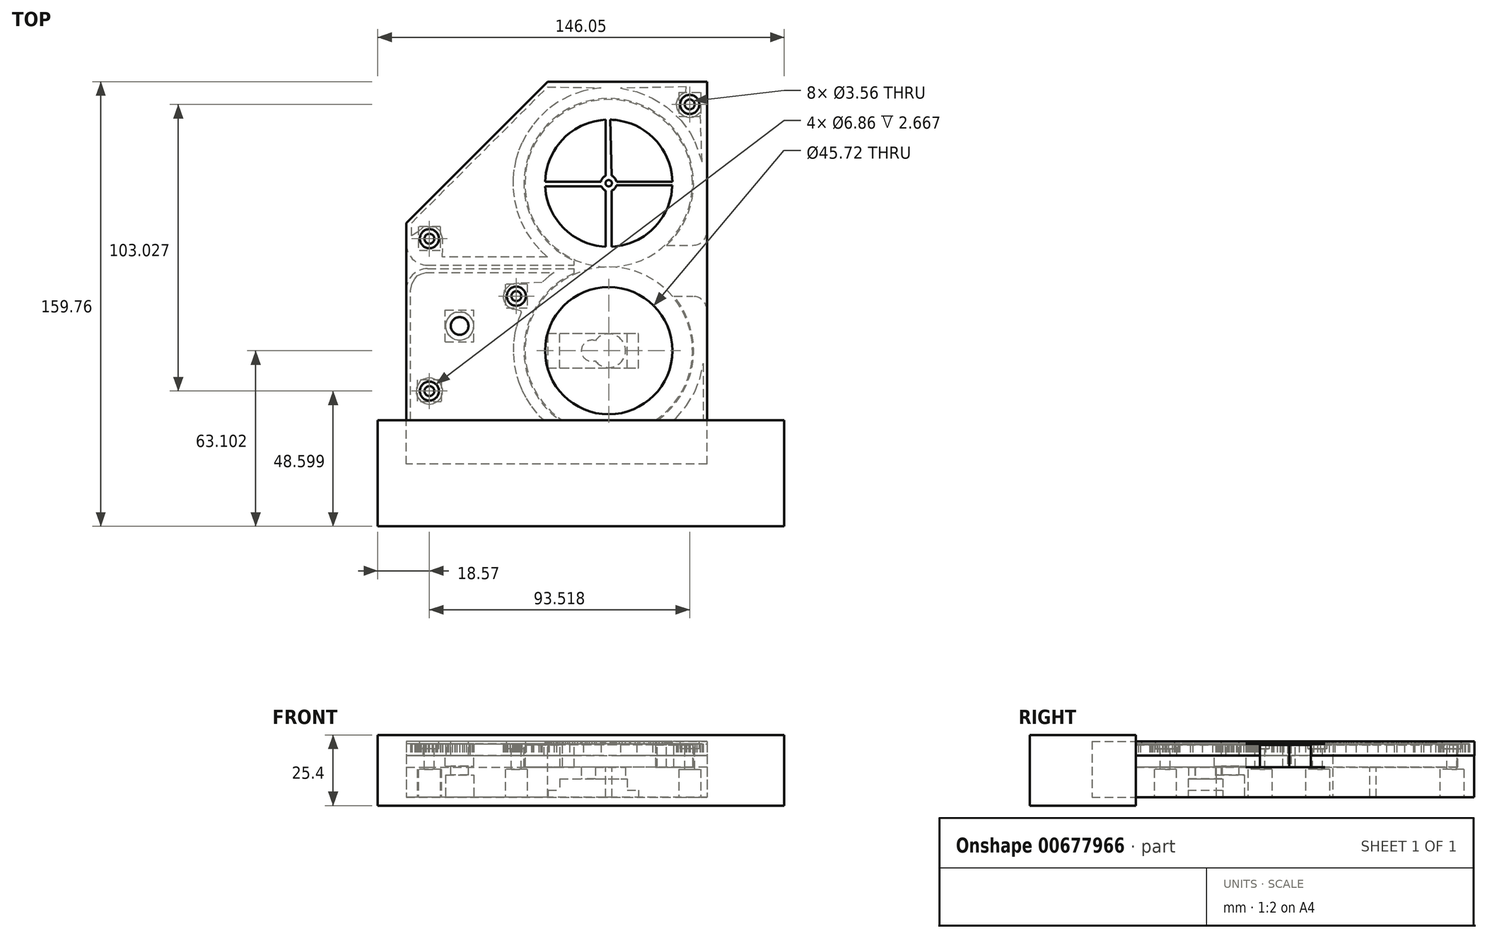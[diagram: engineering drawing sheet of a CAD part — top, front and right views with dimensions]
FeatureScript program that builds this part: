
annotation { "Feature Type Name" : "Feature", "Feature Type Description" : "" }
export const myFeature = defineFeature(function(context is Context, id is Id, definition is map)
    precondition{}
    {
        {
            var Q0;
            Q0=qCreatedBy(makeId("Top.planeOp"),FACE);
            var sketch = newSketch(context, id + "F0", { "sketchPlane" : qUnion([Q0])});
            skLineSegment(sketch, "E0.bottom", {"start": v(35.3, 36.28) * mm, "end": v(-72.74, 36.28) * mm});
            skLineSegment(sketch, "E0.top", {"start": v(35.3, -100.69) * mm, "end": v(-72.74, -100.69) * mm});
            skLineSegment(sketch, "E0.left", {"start": v(35.3, 36.28) * mm, "end": v(35.3, -100.69) * mm});
            skLineSegment(sketch, "E0.right", {"start": v(-72.74, 36.28) * mm, "end": v(-72.74, -100.69) * mm});
            skSolve(sketch);
        }
        {
            var Q0;
            Q0 = qSketchRegion(id + "F0", true);
            extrude(context, id + "F1", {"entities" : qUnion([Q0]), "depth" : 5.08 * mm, "offsetDistance" : 25.4 * mm});
        }
        {
            var Q0;
            {var subQ0=sQuery(id+"F0.wireOp",EDGE,"E0.right");var subQ1=sQuery(id+"F0.wireOp",EDGE,"E0.left");var subQ2=sQuery(id+"F0.wireOp",EDGE,"E0.top");Q0=makeQuery(id+"Ft3egFjg6mGKuU7_1.boolean.opBoolean","SPLIT",FACE,{"disambiguationData":[TD([makeQuery(id+"F1.opExtrude","SWEPT_FACE",FACE,{"disambiguationData":[OSD([subQ2])]})])],"derivedFrom":makeQuery(id+"F1.opExtrude","CAP_FACE",FACE,{"disambiguationData":[OSD([sQuery(id+"F0.wireOp",EDGE,"E0.bottom"),subQ2,subQ1,subQ0])],"isStart":false})});}
            var sketch = newSketch(context, id + "F2", { "sketchPlane" : qUnion([Q0])});
            skLineSegment(sketch, "E1.bottom", {"start": v(-72.74, -100.69) * mm, "end": v(35.3, -100.69) * mm});
            skLineSegment(sketch, "E1.top", {"start": v(-72.74, 36.46) * mm, "end": v(35.3, 36.46) * mm});
            skLineSegment(sketch, "E1.left", {"start": v(-72.74, -100.69) * mm, "end": v(-72.74, 36.46) * mm});
            skLineSegment(sketch, "E1.right", {"start": v(35.3, -100.69) * mm, "end": v(35.3, 36.46) * mm});
            skSolve(sketch);
        }
        {
            var Q0;
            Q0 = qSketchRegion(id + "F2", true);
            extrude(context, id + "F3", {"entities" : qUnion([Q0]), "depth" : 5.08 * mm, "offsetDistance" : 25.4 * mm});
        }
        {
            var Q0;
            Q0=makeQuery(id+"F1.opExtrude","CAP_FACE",FACE,{"disambiguationData":[OSD([sQuery(id+"F0.wireOp",EDGE,"E0.bottom"),sQuery(id+"F0.wireOp",EDGE,"E0.top"),sQuery(id+"F0.wireOp",EDGE,"E0.left"),sQuery(id+"F0.wireOp",EDGE,"E0.right")])],"isStart":false});
            var sketch = newSketch(context, id + "F4", { "sketchPlane" : qUnion([Q0])});
            skCircle(sketch, "E2", {"center": v(0, 0) * mm, "radius": 30.48 * mm});
            skCircle(sketch, "E3", {"center": v(0, -60.2) * mm, "radius": 30.48 * mm});
            skLineSegment(sketch, "E4", {"start": v(0, 0) * mm, "end": v(0, -60.2) * mm});
            skSolve(sketch);
        }
        {
            var Q0;
            Q0 = qSketchRegion(id + "F4", true);
            extrude(context, id + "F5", {"entities" : qUnion([Q0]), "operationType" : NewBodyOperationType.REMOVE, "endBound" : BoundingType.SYMMETRIC, "oppositeDirection" : true, "depth" : 8.38 * mm, "offsetDistance" : 25.4 * mm});
        }
        {
            var Q0;
            Q0=makeQuery(id+"F1.opExtrude","SWEPT_EDGE",EDGE,{"disambiguationData":[OSD([sQuery(id+"F0.wireOp",EDGE,"E0.bottom"),sQuery(id+"F0.wireOp",EDGE,"E0.right")])]});
            chamfer(context, id + "F6", {"entities" : qUnion([Q0]), "width" : 50.8 * mm, "tangentPropagation" : true});
        }
        {
            var Q0;
            Q0=makeQuery(id+"F5.boolean.opBoolean","COPY",FACE,{"derivedFrom":makeQuery(id+"F5.opExtrude","CAP_FACE",FACE,{"disambiguationData":[OSD([sQuery(id+"F4.wireOp",EDGE,"E2")])],"isStart":false})});
            var sketch = newSketch(context, id + "F7", { "sketchPlane" : qUnion([Q0])});
            skCircle(sketch, "E5", {"center": v(0, 0) * mm, "radius": 1.14 * mm});
            skCircle(sketch, "E6", {"center": v(0, -60.2) * mm, "radius": 5.08 * mm});
            skLineSegment(sketch, "E7", {"start": v(0, 0) * mm, "end": v(0, -60.2) * mm});
            skSolve(sketch);
        }
        {
            var Q0;
            Q0 = qSketchRegion(id + "F7", true);
            extrude(context, id + "F8", {"entities" : qUnion([Q0]), "operationType" : NewBodyOperationType.REMOVE, "endBound" : BoundingType.SYMMETRIC, "oppositeDirection" : true, "depth" : 25.4 * mm, "offsetDistance" : 25.4 * mm});
        }
        {
            var Q0;
            Q0=makeQuery(id+"F3.opExtrude","SWEPT_EDGE",EDGE,{"disambiguationData":[OSD([sQuery(id+"F2.wireOp",EDGE,"E1.top"),sQuery(id+"F2.wireOp",EDGE,"E1.left")])]});
            chamfer(context, id + "F9", {"entities" : qUnion([Q0]), "width" : 50.8 * mm, "tangentPropagation" : true});
        }
        {
            var Q0;
            {var subQ0=sQuery(id+"F0.wireOp",EDGE,"E0.right");var subQ1=sQuery(id+"F0.wireOp",EDGE,"E0.left");var subQ2=sQuery(id+"F0.wireOp",EDGE,"E0.bottom");var subQ3=makeQuery(id+"F1.opExtrude","CAP_FACE",FACE,{"disambiguationData":[OSD([subQ2,sQuery(id+"F0.wireOp",EDGE,"E0.top"),subQ1,subQ0])],"isStart":false});Q0=makeQuery(id+"FFet9ike0QdHDJR_2.boolean.opBoolean","SPLIT",FACE,{"disambiguationData":[TD([makeQuery(id+"F1.opExtrude","SWEPT_FACE",FACE,{"disambiguationData":[OSD([subQ2])]})])],"derivedFrom":subQ3});}
            var sketch = newSketch(context, id + "F10", { "sketchPlane" : qUnion([Q0])});
            skLineSegment(sketch, "E8.bottom", {"start": v(0, -22.29) * mm, "end": v(46.56, -22.29) * mm});
            skLineSegment(sketch, "E8.top", {"start": v(0, -40.66) * mm, "end": v(46.56, -40.66) * mm});
            skLineSegment(sketch, "E8.left", {"start": v(0, -22.29) * mm, "end": v(0, -40.66) * mm});
            skLineSegment(sketch, "E8.right", {"start": v(46.56, -22.29) * mm, "end": v(46.56, -40.66) * mm});
            skLineSegment(sketch, "E9.bottom", {"start": v(2.73, -33.02) * mm, "end": v(-12.34, -33.02) * mm});
            skLineSegment(sketch, "E9.top", {"start": v(2.73, -27.18) * mm, "end": v(-12.34, -27.18) * mm});
            skLineSegment(sketch, "E9.left", {"start": v(2.73, -33.02) * mm, "end": v(2.73, -27.18) * mm});
            skLineSegment(sketch, "E9.right", {"start": v(-12.34, -33.02) * mm, "end": v(-12.34, -27.18) * mm});
            skPoint(sketch, "E9.middle", {"position": v(-4.8, -30.1) * mm});
            skSolve(sketch);
        }
        {
            var Q0;
            Q0 = qSketchRegion(id + "F10", true);
            extrude(context, id + "F11", {"entities" : qUnion([Q0]), "operationType" : NewBodyOperationType.REMOVE, "endBound" : BoundingType.SYMMETRIC, "oppositeDirection" : true, "depth" : 8.38 * mm, "offsetDistance" : 25.4 * mm});
        }
        {
            var Q0;
            Q0=makeQuery(id+"F1.opExtrude","CAP_FACE",FACE,{"disambiguationData":[OSD([sQuery(id+"F0.wireOp",EDGE,"E0.bottom"),sQuery(id+"F0.wireOp",EDGE,"E0.top"),sQuery(id+"F0.wireOp",EDGE,"E0.left"),sQuery(id+"F0.wireOp",EDGE,"E0.right")])],"isStart":true});
            extrude(context, id + "F12", {"entities" : qUnion([Q0]), "operationType" : NewBodyOperationType.ADD, "depth" : 9.9 * mm, "offsetDistance" : 25.4 * mm});
        }
        {
            var Q0;
            Q0=makeQuery(id+"F12.opExtrude","CAP_FACE",FACE,{"disambiguationData":[OSD([sQuery(id+"F0.wireOp",EDGE,"E0.bottom"),sQuery(id+"F0.wireOp",EDGE,"E0.top"),sQuery(id+"F0.wireOp",EDGE,"E0.left"),sQuery(id+"F0.wireOp",EDGE,"E0.right")])],"isStart":false});
            var sketch = newSketch(context, id + "F13", { "sketchPlane" : qUnion([Q0])});
            skPoint(sketch, "E10.middle", {"position": v(0, 60.2) * mm});
            skLineSegment(sketch, "E11", {"start": v(0, 60.2) * mm, "end": v(-5.49, 60.2) * mm});
            skLineSegment(sketch, "E12.bottom", {"start": v(-21.74, 66.42) * mm, "end": v(10.77, 66.42) * mm});
            skLineSegment(sketch, "E12.top", {"start": v(-21.74, 53.98) * mm, "end": v(10.77, 53.98) * mm});
            skLineSegment(sketch, "E12.left", {"start": v(-21.74, 66.42) * mm, "end": v(-21.74, 53.98) * mm});
            skLineSegment(sketch, "E12.right", {"start": v(10.77, 66.42) * mm, "end": v(10.77, 53.98) * mm});
            skPoint(sketch, "E12.middle", {"position": v(-5.49, 60.2) * mm});
            skSolve(sketch);
        }
        {
            var Q0;
            Q0 = qSketchRegion(id + "F13", true);
            extrude(context, id + "F14", {"entities" : qUnion([Q0]), "operationType" : NewBodyOperationType.REMOVE, "oppositeDirection" : true, "depth" : 2.54 * mm, "offsetDistance" : 25.4 * mm});
        }
        {
            var Q0;
            Q0=makeQuery(id+"F14.boolean.opBoolean","COPY",FACE,{"derivedFrom":makeQuery(id+"F14.opExtrude","CAP_FACE",FACE,{"disambiguationData":[OSD([sQuery(id+"F13.wireOp",EDGE,"E12.bottom"),sQuery(id+"F13.wireOp",EDGE,"E12.top"),sQuery(id+"F13.wireOp",EDGE,"E12.left"),sQuery(id+"F13.wireOp",EDGE,"E12.right")])],"isStart":false})});
            var sketch = newSketch(context, id + "F15", { "sketchPlane" : qUnion([Q0])});
            skCircle(sketch, "E13", {"center": v(0, 60.2) * mm, "radius": 6.03 * mm});
            skCircle(sketch, "E14", {"center": v(-6.03, 60.2) * mm, "radius": 3.81 * mm});
            skSolve(sketch);
        }
        {
            var Q0;
            Q0 = qSketchRegion(id + "F15", true);
            extrude(context, id + "F16", {"entities" : qUnion([Q0]), "operationType" : NewBodyOperationType.REMOVE, "oppositeDirection" : true, "depth" : 25.4 * mm, "offsetDistance" : 25.4 * mm});
        }
        {
            var Q0;
            {var subQ0=sQuery(id+"F0.wireOp",EDGE,"E0.right");var subQ1=sQuery(id+"F0.wireOp",EDGE,"E0.left");var subQ2=sQuery(id+"F0.wireOp",EDGE,"E0.top");var subQ3=makeQuery(id+"F1.opExtrude","CAP_FACE",FACE,{"disambiguationData":[OSD([sQuery(id+"F0.wireOp",EDGE,"E0.bottom"),subQ2,subQ1,subQ0])],"isStart":false});Q0=makeQuery(id+"FFet9ike0QdHDJR_2.boolean.opBoolean","SPLIT",FACE,{"disambiguationData":[TD([makeQuery(id+"F1.opExtrude","SWEPT_FACE",FACE,{"disambiguationData":[OSD([subQ2])]})])],"derivedFrom":subQ3});}
            var sketch = newSketch(context, id + "F17", { "sketchPlane" : qUnion([Q0])});
            skCircle(sketch, "E15", {"center": v(-33.19, -40.6) * mm, "radius": 1.78 * mm});
            skCircle(sketch, "E16", {"center": v(29.09, 28.33) * mm, "radius": 1.78 * mm});
            skCircle(sketch, "E17", {"center": v(-53.56, -51.3) * mm, "radius": 3.18 * mm});
            skCircle(sketch, "E18", {"center": v(-64.43, -19.95) * mm, "radius": 1.78 * mm});
            skCircle(sketch, "E19", {"center": v(-64.43, -74.7) * mm, "radius": 1.78 * mm});
            skSolve(sketch);
        }
        {
            var Q0;
            Q0 = qSketchRegion(id + "F17", true);
            extrude(context, id + "F18", {"entities" : qUnion([Q0]), "operationType" : NewBodyOperationType.REMOVE, "endBound" : BoundingType.SYMMETRIC, "oppositeDirection" : true, "depth" : 50.8 * mm, "offsetDistance" : 25.4 * mm});
        }
        {
            var Q0;
            Q0=makeQuery(id+"F3.opExtrude","CAP_FACE",FACE,{"disambiguationData":[OSD([sQuery(id+"F2.wireOp",EDGE,"E1.bottom"),sQuery(id+"F2.wireOp",EDGE,"E1.top"),sQuery(id+"F2.wireOp",EDGE,"E1.left"),sQuery(id+"F2.wireOp",EDGE,"E1.right")])],"isStart":false});
            var sketch = newSketch(context, id + "F19", { "sketchPlane" : qUnion([Q0])});
            skCircle(sketch, "E20", {"center": v(-33.19, -40.6) * mm, "radius": 3.43 * mm});
            skCircle(sketch, "E21", {"center": v(29.09, 28.33) * mm, "radius": 3.43 * mm});
            skCircle(sketch, "E22", {"center": v(-64.43, -19.95) * mm, "radius": 3.43 * mm});
            skCircle(sketch, "E23", {"center": v(-64.43, -74.7) * mm, "radius": 3.43 * mm});
            skSolve(sketch);
        }
        {
            var Q0;
            Q0 = qSketchRegion(id + "F19", true);
            extrude(context, id + "F20", {"entities" : qUnion([Q0]), "operationType" : NewBodyOperationType.REMOVE, "oppositeDirection" : true, "depth" : 2.67 * mm, "offsetDistance" : 25.4 * mm});
        }
        {
            var Q0;
            Q0=makeQuery(id+"F12.opExtrude","CAP_FACE",FACE,{"disambiguationData":[OSD([sQuery(id+"F0.wireOp",EDGE,"E0.bottom"),sQuery(id+"F0.wireOp",EDGE,"E0.top"),sQuery(id+"F0.wireOp",EDGE,"E0.left"),sQuery(id+"F0.wireOp",EDGE,"E0.right")])],"isStart":false});
            var sketch = newSketch(context, id + "F21", { "sketchPlane" : qUnion([Q0])});
            skLineSegment(sketch, "E24.bottom", {"start": v(-29.25, 36.28) * mm, "end": v(-37.13, 36.28) * mm});
            skLineSegment(sketch, "E24.top", {"start": v(-29.25, 44.91) * mm, "end": v(-37.13, 44.91) * mm});
            skLineSegment(sketch, "E24.left", {"start": v(-29.25, 36.28) * mm, "end": v(-29.25, 44.91) * mm});
            skLineSegment(sketch, "E24.right", {"start": v(-37.13, 36.28) * mm, "end": v(-37.13, 44.91) * mm});
            skPoint(sketch, "E24.middle", {"position": v(-33.19, 40.6) * mm});
            skLineSegment(sketch, "E25.bottom", {"start": v(-37.13, 36.28) * mm, "end": v(-29.25, 36.28) * mm});
            skLineSegment(sketch, "E25.top", {"start": v(-37.13, 44.91) * mm, "end": v(-29.25, 44.91) * mm});
            skLineSegment(sketch, "E26.bottom", {"start": v(25.15, -32.64) * mm, "end": v(33.02, -32.64) * mm});
            skLineSegment(sketch, "E26.top", {"start": v(25.15, -24) * mm, "end": v(33.02, -24) * mm});
            skLineSegment(sketch, "E26.left", {"start": v(25.15, -32.64) * mm, "end": v(25.15, -24) * mm});
            skLineSegment(sketch, "E26.right", {"start": v(33.02, -32.64) * mm, "end": v(33.02, -24) * mm});
            skPoint(sketch, "E26.middle", {"position": v(29.09, -28.33) * mm});
            skLineSegment(sketch, "E27.bottom", {"start": v(-60.11, 70.76) * mm, "end": v(-68.75, 70.76) * mm});
            skLineSegment(sketch, "E27.top", {"start": v(-60.11, 78.64) * mm, "end": v(-68.75, 78.64) * mm});
            skLineSegment(sketch, "E27.left", {"start": v(-60.11, 70.76) * mm, "end": v(-60.11, 78.64) * mm});
            skLineSegment(sketch, "E27.right", {"start": v(-68.75, 70.76) * mm, "end": v(-68.75, 78.64) * mm});
            skPoint(sketch, "E27.middle", {"position": v(-64.43, 74.7) * mm});
            skLineSegment(sketch, "E28.bottom", {"start": v(-60.5, 15.63) * mm, "end": v(-68.37, 15.63) * mm});
            skLineSegment(sketch, "E28.top", {"start": v(-60.5, 24.27) * mm, "end": v(-68.37, 24.27) * mm});
            skLineSegment(sketch, "E28.left", {"start": v(-60.5, 15.63) * mm, "end": v(-60.5, 24.27) * mm});
            skLineSegment(sketch, "E28.right", {"start": v(-68.37, 15.63) * mm, "end": v(-68.37, 24.27) * mm});
            skPoint(sketch, "E28.middle", {"position": v(-64.43, 19.95) * mm});
            skSolve(sketch);
        }
        {
            var Q0;
            Q0 = qSketchRegion(id + "F21", true);
            extrude(context, id + "F22", {"entities" : qUnion([Q0]), "operationType" : NewBodyOperationType.REMOVE, "oppositeDirection" : true, "depth" : 10.03 * mm, "offsetDistance" : 25.4 * mm});
        }
        {
            var Q0;
            Q0=makeQuery(id+"F12.opExtrude","CAP_FACE",FACE,{"disambiguationData":[OSD([sQuery(id+"F0.wireOp",EDGE,"E0.bottom"),sQuery(id+"F0.wireOp",EDGE,"E0.top"),sQuery(id+"F0.wireOp",EDGE,"E0.left"),sQuery(id+"F0.wireOp",EDGE,"E0.right")])],"isStart":false});
            var sketch = newSketch(context, id + "F23", { "sketchPlane" : qUnion([Q0])});
            skCircle(sketch, "E29", {"center": v(-53.56, 51.3) * mm, "radius": 5.08 * mm});
            skSolve(sketch);
        }
        {
            var Q0;
            Q0 = qSketchRegion(id + "F23", true);
            extrude(context, id + "F24", {"entities" : qUnion([Q0]), "operationType" : NewBodyOperationType.REMOVE, "oppositeDirection" : true, "depth" : 8 * mm, "offsetDistance" : 25.4 * mm});
        }
        {
            var Q0;
            {var subQ0=sQuery(id+"F0.wireOp",EDGE,"E0.right");var subQ1=sQuery(id+"F0.wireOp",EDGE,"E0.left");var subQ2=sQuery(id+"F0.wireOp",EDGE,"E0.top");var subQ3=makeQuery(id+"F1.opExtrude","CAP_FACE",FACE,{"disambiguationData":[OSD([sQuery(id+"F0.wireOp",EDGE,"E0.bottom"),subQ2,subQ1,subQ0])],"isStart":false});Q0=makeQuery(id+"FFet9ike0QdHDJR_2.boolean.opBoolean","SPLIT",FACE,{"disambiguationData":[TD([makeQuery(id+"F1.opExtrude","SWEPT_FACE",FACE,{"disambiguationData":[OSD([subQ2])]})])],"derivedFrom":subQ3});}
            var sketch = newSketch(context, id + "F25", { "sketchPlane" : qUnion([Q0])});
            skLineSegment(sketch, "E30.bottom", {"start": v(-58.7, -57.02) * mm, "end": v(-48.41, -57.02) * mm});
            skLineSegment(sketch, "E30.top", {"start": v(-58.7, -45.6) * mm, "end": v(-48.41, -45.6) * mm});
            skLineSegment(sketch, "E30.left", {"start": v(-58.7, -57.02) * mm, "end": v(-58.7, -45.6) * mm});
            skLineSegment(sketch, "E30.right", {"start": v(-48.41, -57.02) * mm, "end": v(-48.41, -45.6) * mm});
            skPoint(sketch, "E30.middle", {"position": v(-53.56, -51.3) * mm});
            skSolve(sketch);
        }
        {
            var Q0;
            Q0 = qSketchRegion(id + "F25", true);
            extrude(context, id + "F26", {"entities" : qUnion([Q0]), "operationType" : NewBodyOperationType.REMOVE, "oppositeDirection" : true, "depth" : 3.8 * mm, "offsetDistance" : 25.4 * mm});
        }
        {
            var Q0;
            Q0=makeQuery(id+"F11.boolean.opBoolean","INTERSECT",EDGE,{"derivedFrom":[makeQuery(id+"F1.opExtrude","SWEPT_FACE",FACE,{"disambiguationData":[OSD([sQuery(id+"F0.wireOp",EDGE,"E0.left")])]}),makeQuery(id+"F11.opExtrude","SWEPT_FACE",FACE,{"disambiguationData":[OSD([sQuery(id+"F10.wireOp",EDGE,"E8.top")])]})]});
            var Q1;
            Q1=makeQuery(id+"F11.boolean.opBoolean","INTERSECT",EDGE,{"derivedFrom":[makeQuery(id+"F3.opExtrude","SWEPT_FACE",FACE,{"disambiguationData":[OSD([sQuery(id+"F2.wireOp",EDGE,"E1.right")])]}),makeQuery(id+"F11.opExtrude","SWEPT_FACE",FACE,{"disambiguationData":[OSD([sQuery(id+"F10.wireOp",EDGE,"E8.top")])]})]});
            var Q2;
            Q2=makeQuery(id+"F11.boolean.opBoolean","INTERSECT",EDGE,{"derivedFrom":[makeQuery(id+"F3.opExtrude","SWEPT_FACE",FACE,{"disambiguationData":[OSD([sQuery(id+"F2.wireOp",EDGE,"E1.right")])]}),makeQuery(id+"F11.opExtrude","SWEPT_FACE",FACE,{"disambiguationData":[OSD([sQuery(id+"F10.wireOp",EDGE,"E8.bottom")])]})]});
            var Q3;
            Q3=makeQuery(id+"F11.boolean.opBoolean","INTERSECT",EDGE,{"derivedFrom":[makeQuery(id+"F1.opExtrude","SWEPT_FACE",FACE,{"disambiguationData":[OSD([sQuery(id+"F0.wireOp",EDGE,"E0.left")])]}),makeQuery(id+"F11.opExtrude","SWEPT_FACE",FACE,{"disambiguationData":[OSD([sQuery(id+"F10.wireOp",EDGE,"E8.bottom")])]})]});
            fillet(context, id + "F27", {"entities" : qUnion([Q0, Q1, Q2, Q3]), "radius" : 5.08 * mm, "tangentPropagation" : true, "allowEdgeOverflow" : false});
        }
        {
            var Q0;
            Q0=makeQuery(id+"F14.boolean.opBoolean","COPY",FACE,{"derivedFrom":makeQuery(id+"F14.opExtrude","CAP_FACE",FACE,{"disambiguationData":[OSD([sQuery(id+"F13.wireOp",EDGE,"E12.bottom"),sQuery(id+"F13.wireOp",EDGE,"E12.top"),sQuery(id+"F13.wireOp",EDGE,"E12.left"),sQuery(id+"F13.wireOp",EDGE,"E12.right")])],"isStart":false})});
            var sketch = newSketch(context, id + "F28", { "sketchPlane" : qUnion([Q0])});
            skLineSegment(sketch, "E31.bottom", {"start": v(6.65, 66.42) * mm, "end": v(-17.62, 66.42) * mm});
            skLineSegment(sketch, "E31.top", {"start": v(6.65, 53.98) * mm, "end": v(-17.62, 53.98) * mm});
            skLineSegment(sketch, "E31.left", {"start": v(6.65, 66.42) * mm, "end": v(6.65, 53.98) * mm});
            skLineSegment(sketch, "E31.right", {"start": v(-17.62, 66.42) * mm, "end": v(-17.62, 53.98) * mm});
            skPoint(sketch, "E31.middle", {"position": v(-5.49, 60.2) * mm});
            skPoint(sketch, "E31.middle.positionSnap0", {"position": v(10.77, 60.2) * mm});
            skPoint(sketch, "E31.middle.positionSnap1", {"position": v(-5.49, 53.98) * mm});
            skPoint(sketch, "E31.centerSnap0", {"position": v(10.77, 60.2) * mm});
            skPoint(sketch, "E31.centerSnap1", {"position": v(-5.49, 53.98) * mm});
            skSolve(sketch);
        }
        {
            var Q0;
            Q0=makeQuery(id+"F1.opExtrude","CAP_FACE",FACE,{"disambiguationData":[OSD([sQuery(id+"F0.wireOp",EDGE,"E0.bottom"),sQuery(id+"F0.wireOp",EDGE,"E0.top"),sQuery(id+"F0.wireOp",EDGE,"E0.left"),sQuery(id+"F0.wireOp",EDGE,"E0.right")])],"isStart":false});
            var sketch = newSketch(context, id + "F29", { "sketchPlane" : qUnion([Q0])});
            skLineSegment(sketch, "E32", {"start": v(0, 0) * mm, "end": v(0, -30.1) * mm});
            skLineSegment(sketch, "E33.bottom", {"start": v(-84.33, -30.73) * mm, "end": v(84.33, -30.73) * mm});
            skLineSegment(sketch, "E33.top", {"start": v(-84.33, -29.46) * mm, "end": v(84.33, -29.46) * mm});
            skLineSegment(sketch, "E33.left", {"start": v(-84.33, -30.73) * mm, "end": v(-84.33, -29.46) * mm});
            skLineSegment(sketch, "E33.right", {"start": v(84.33, -30.73) * mm, "end": v(84.33, -29.46) * mm});
            skPoint(sketch, "E33.middle", {"position": v(0, -30.1) * mm});
            skSolve(sketch);
        }
        {
            var Q0;
            Q0 = qSketchRegion(id + "F29", true);
            extrude(context, id + "F30", {"entities" : qUnion([Q0]), "operationType" : NewBodyOperationType.REMOVE, "endBound" : BoundingType.SYMMETRIC, "oppositeDirection" : true, "depth" : 8.38 * mm, "offsetDistance" : 25.4 * mm});
        }
        {
            var Q0;
            Q0 = qSketchRegion(id + "F28", true);
            extrude(context, id + "F31", {"entities" : qUnion([Q0]), "operationType" : NewBodyOperationType.REMOVE, "oppositeDirection" : true, "depth" : 4.06 * mm, "offsetDistance" : 25.4 * mm});
        }
        {
            var Q0;
            Q0=makeQuery(id+"F3.opExtrude","CAP_FACE",FACE,{"disambiguationData":[OSD([sQuery(id+"F2.wireOp",EDGE,"E1.bottom"),sQuery(id+"F2.wireOp",EDGE,"E1.top"),sQuery(id+"F2.wireOp",EDGE,"E1.left"),sQuery(id+"F2.wireOp",EDGE,"E1.right")])],"isStart":false});
            var sketch = newSketch(context, id + "F32", { "sketchPlane" : qUnion([Q0])});
            skCircle(sketch, "E34", {"center": v(0, -60.2) * mm, "radius": 22.86 * mm});
            skLineSegment(sketch, "E35", {"start": v(-2.8, 0.55) * mm, "end": v(-22.85, 0.55) * mm});
            skLineSegment(sketch, "E36", {"start": v(-22.85, 0.55) * mm, "end": v(-22.75, 2.25) * mm});
            skLineSegment(sketch, "E37", {"start": v(-22.75, 2.25) * mm, "end": v(-22.56, 3.67) * mm});
            skLineSegment(sketch, "E38", {"start": v(-22.56, 3.67) * mm, "end": v(-22.23, 5.33) * mm});
            skLineSegment(sketch, "E39", {"start": v(-22.23, 5.33) * mm, "end": v(-21.79, 6.91) * mm});
            skLineSegment(sketch, "E40", {"start": v(-21.79, 6.91) * mm, "end": v(-21.18, 8.6) * mm});
            skLineSegment(sketch, "E41", {"start": v(-21.18, 8.6) * mm, "end": v(-20.43, 10.25) * mm});
            skLineSegment(sketch, "E42", {"start": v(-20.43, 10.25) * mm, "end": v(-19.68, 11.63) * mm});
            skLineSegment(sketch, "E43", {"start": v(-19.68, 11.63) * mm, "end": v(-18.94, 12.8) * mm});
            skLineSegment(sketch, "E44", {"start": v(-18.94, 12.8) * mm, "end": v(-18.14, 13.9) * mm});
            skLineSegment(sketch, "E45", {"start": v(-18.14, 13.9) * mm, "end": v(-16.73, 15.58) * mm});
            skLineSegment(sketch, "E46", {"start": v(-16.73, 15.58) * mm, "end": v(-15.43, 16.87) * mm});
            skLineSegment(sketch, "E47", {"start": v(-15.43, 16.87) * mm, "end": v(-14.02, 18.06) * mm});
            skLineSegment(sketch, "E48", {"start": v(-14.02, 18.06) * mm, "end": v(-12.1, 19.39) * mm});
            skLineSegment(sketch, "E49", {"start": v(-12.1, 19.39) * mm, "end": v(-9.94, 20.59) * mm});
            skLineSegment(sketch, "E50", {"start": v(-9.94, 20.59) * mm, "end": v(-8.4, 21.26) * mm});
            skLineSegment(sketch, "E51", {"start": v(-8.4, 21.26) * mm, "end": v(-6.92, 21.79) * mm});
            skLineSegment(sketch, "E52", {"start": v(-6.92, 21.79) * mm, "end": v(-5.08, 22.29) * mm});
            skLineSegment(sketch, "E53", {"start": v(-5.08, 22.29) * mm, "end": v(-2.91, 22.67) * mm});
            skLineSegment(sketch, "E54", {"start": v(-2.91, 22.67) * mm, "end": v(-1.1, 22.83) * mm});
            skLineSegment(sketch, "E55", {"start": v(-1.1, 22.83) * mm, "end": v(-1.1, 2.64) * mm});
            skLineSegment(sketch, "E56", {"start": v(-1.1, 2.64) * mm, "end": v(-1.43, 2.47) * mm});
            skLineSegment(sketch, "E57", {"start": v(-1.43, 2.47) * mm, "end": v(-1.74, 2.27) * mm});
            skLineSegment(sketch, "E58", {"start": v(-1.74, 2.27) * mm, "end": v(-2.08, 1.96) * mm});
            skLineSegment(sketch, "E59", {"start": v(-2.08, 1.96) * mm, "end": v(-2.38, 1.59) * mm});
            skLineSegment(sketch, "E60", {"start": v(-2.38, 1.59) * mm, "end": v(-2.6, 1.17) * mm});
            skLineSegment(sketch, "E61", {"start": v(-2.6, 1.17) * mm, "end": v(-2.7, 0.9) * mm});
            skLineSegment(sketch, "E62", {"start": v(-2.7, 0.9) * mm, "end": v(-2.8, 0.55) * mm});
            skLineSegment(sketch, "E63", {"start": v(2.8, 0.55) * mm, "end": v(22.85, 0.55) * mm});
            skLineSegment(sketch, "E64", {"start": v(22.85, 0.55) * mm, "end": v(22.78, 1.89) * mm});
            skLineSegment(sketch, "E65", {"start": v(22.78, 1.89) * mm, "end": v(22.6, 3.39) * mm});
            skLineSegment(sketch, "E66", {"start": v(22.6, 3.39) * mm, "end": v(22.2, 5.44) * mm});
            skLineSegment(sketch, "E67", {"start": v(22.2, 5.44) * mm, "end": v(21.59, 7.53) * mm});
            skLineSegment(sketch, "E68", {"start": v(21.59, 7.53) * mm, "end": v(20.9, 9.27) * mm});
            skLineSegment(sketch, "E69", {"start": v(20.9, 9.27) * mm, "end": v(20.07, 10.94) * mm});
            skLineSegment(sketch, "E70", {"start": v(20.07, 10.94) * mm, "end": v(19.26, 12.32) * mm});
            skLineSegment(sketch, "E71", {"start": v(19.26, 12.32) * mm, "end": v(18.21, 13.82) * mm});
            skLineSegment(sketch, "E72", {"start": v(18.21, 13.82) * mm, "end": v(17.27, 14.98) * mm});
            skLineSegment(sketch, "E73", {"start": v(17.27, 14.98) * mm, "end": v(16.1, 16.23) * mm});
            skLineSegment(sketch, "E74", {"start": v(16.1, 16.23) * mm, "end": v(14.47, 17.7) * mm});
            skLineSegment(sketch, "E75", {"start": v(14.47, 17.7) * mm, "end": v(12.73, 19) * mm});
            skLineSegment(sketch, "E76", {"start": v(12.73, 19) * mm, "end": v(11.2, 19.93) * mm});
            skLineSegment(sketch, "E77", {"start": v(11.2, 19.93) * mm, "end": v(9.5, 20.8) * mm});
            skLineSegment(sketch, "E78", {"start": v(9.5, 20.8) * mm, "end": v(7.95, 21.43) * mm});
            skLineSegment(sketch, "E79", {"start": v(7.95, 21.43) * mm, "end": v(6.05, 22.04) * mm});
            skLineSegment(sketch, "E80", {"start": v(6.05, 22.04) * mm, "end": v(3.83, 22.54) * mm});
            skLineSegment(sketch, "E81", {"start": v(3.83, 22.54) * mm, "end": v(2.63, 22.7) * mm});
            skLineSegment(sketch, "E82", {"start": v(2.63, 22.7) * mm, "end": v(1.41, 22.82) * mm});
            skLineSegment(sketch, "E83", {"start": v(1.41, 22.82) * mm, "end": v(0.75, 22.85) * mm});
            skLineSegment(sketch, "E84", {"start": v(0.75, 22.85) * mm, "end": v(0.55, 22.85) * mm});
            skLineSegment(sketch, "E85", {"start": v(0.55, 22.85) * mm, "end": v(1.1, 2.64) * mm});
            skLineSegment(sketch, "E86", {"start": v(1.1, 2.64) * mm, "end": v(1.41, 2.5) * mm});
            skLineSegment(sketch, "E87", {"start": v(1.41, 2.5) * mm, "end": v(1.68, 2.31) * mm});
            skLineSegment(sketch, "E88", {"start": v(1.68, 2.31) * mm, "end": v(2, 2.04) * mm});
            skLineSegment(sketch, "E89", {"start": v(2, 2.04) * mm, "end": v(2.27, 1.74) * mm});
            skLineSegment(sketch, "E90", {"start": v(2.27, 1.74) * mm, "end": v(2.5, 1.37) * mm});
            skLineSegment(sketch, "E91", {"start": v(2.5, 1.37) * mm, "end": v(2.73, 0.85) * mm});
            skLineSegment(sketch, "E92", {"start": v(2.73, 0.85) * mm, "end": v(2.8, 0.55) * mm});
            skLineSegment(sketch, "E93", {"start": v(-1.1, -2.64) * mm, "end": v(-1.1, -22.83) * mm});
            skLineSegment(sketch, "E94", {"start": v(-1.1, -22.83) * mm, "end": v(-2.52, -22.72) * mm});
            skLineSegment(sketch, "E95", {"start": v(-2.52, -22.72) * mm, "end": v(-4.43, -22.43) * mm});
            skLineSegment(sketch, "E96", {"start": v(-4.43, -22.43) * mm, "end": v(-5.92, -22.08) * mm});
            skLineSegment(sketch, "E97", {"start": v(-5.92, -22.08) * mm, "end": v(-7.74, -21.5) * mm});
            skLineSegment(sketch, "E98", {"start": v(-7.74, -21.5) * mm, "end": v(-9.46, -20.8) * mm});
            skLineSegment(sketch, "E99", {"start": v(-9.46, -20.8) * mm, "end": v(-11.16, -19.95) * mm});
            skLineSegment(sketch, "E100", {"start": v(-11.16, -19.95) * mm, "end": v(-12.95, -18.84) * mm});
            skLineSegment(sketch, "E101", {"start": v(-12.95, -18.84) * mm, "end": v(-14.67, -17.54) * mm});
            skLineSegment(sketch, "E102", {"start": v(-14.67, -17.54) * mm, "end": v(-16.2, -16.13) * mm});
            skLineSegment(sketch, "E103", {"start": v(-16.2, -16.13) * mm, "end": v(-17.46, -14.75) * mm});
            skLineSegment(sketch, "E104", {"start": v(-17.46, -14.75) * mm, "end": v(-18.55, -13.36) * mm});
            skLineSegment(sketch, "E105", {"start": v(-18.55, -13.36) * mm, "end": v(-19.76, -11.49) * mm});
            skLineSegment(sketch, "E106", {"start": v(-19.76, -11.49) * mm, "end": v(-20.78, -9.53) * mm});
            skLineSegment(sketch, "E107", {"start": v(-20.78, -9.53) * mm, "end": v(-21.53, -7.68) * mm});
            skLineSegment(sketch, "E108", {"start": v(-21.53, -7.68) * mm, "end": v(-22.12, -5.75) * mm});
            skLineSegment(sketch, "E109", {"start": v(-22.12, -5.75) * mm, "end": v(-22.53, -3.88) * mm});
            skLineSegment(sketch, "E110", {"start": v(-22.53, -3.88) * mm, "end": v(-22.83, -1.14) * mm});
            skLineSegment(sketch, "E111", {"start": v(-22.83, -1.14) * mm, "end": v(-2.62, -1.14) * mm});
            skLineSegment(sketch, "E112", {"start": v(-2.62, -1.14) * mm, "end": v(-2.4, -1.55) * mm});
            skLineSegment(sketch, "E113", {"start": v(-2.4, -1.55) * mm, "end": v(-2.13, -1.9) * mm});
            skLineSegment(sketch, "E114", {"start": v(-2.13, -1.9) * mm, "end": v(-1.74, -2.26) * mm});
            skLineSegment(sketch, "E115", {"start": v(-1.74, -2.26) * mm, "end": v(-1.44, -2.47) * mm});
            skLineSegment(sketch, "E116", {"start": v(-1.44, -2.47) * mm, "end": v(-1.1, -2.64) * mm});
            skLineSegment(sketch, "E117", {"start": v(1.1, -2.64) * mm, "end": v(1.1, -22.83) * mm});
            skLineSegment(sketch, "E118", {"start": v(1.1, -22.83) * mm, "end": v(2.38, -22.74) * mm});
            skLineSegment(sketch, "E119", {"start": v(2.38, -22.74) * mm, "end": v(4.9, -22.33) * mm});
            skLineSegment(sketch, "E120", {"start": v(4.9, -22.33) * mm, "end": v(7.52, -21.59) * mm});
            skLineSegment(sketch, "E121", {"start": v(7.52, -21.59) * mm, "end": v(10.6, -20.25) * mm});
            skLineSegment(sketch, "E122", {"start": v(10.6, -20.25) * mm, "end": v(12.7, -19) * mm});
            skLineSegment(sketch, "E123", {"start": v(12.7, -19) * mm, "end": v(15.16, -17.11) * mm});
            skLineSegment(sketch, "E124", {"start": v(15.16, -17.11) * mm, "end": v(16.8, -15.5) * mm});
            skLineSegment(sketch, "E125", {"start": v(16.8, -15.5) * mm, "end": v(18.09, -13.98) * mm});
            skLineSegment(sketch, "E126", {"start": v(18.09, -13.98) * mm, "end": v(19.47, -11.97) * mm});
            skLineSegment(sketch, "E127", {"start": v(19.47, -11.97) * mm, "end": v(20.38, -10.35) * mm});
            skLineSegment(sketch, "E128", {"start": v(20.38, -10.35) * mm, "end": v(21.19, -8.58) * mm});
            skLineSegment(sketch, "E129", {"start": v(21.19, -8.58) * mm, "end": v(21.8, -6.91) * mm});
            skLineSegment(sketch, "E130", {"start": v(21.8, -6.91) * mm, "end": v(22.19, -5.5) * mm});
            skLineSegment(sketch, "E131", {"start": v(22.19, -5.5) * mm, "end": v(22.46, -4.27) * mm});
            skLineSegment(sketch, "E132", {"start": v(22.46, -4.27) * mm, "end": v(22.7, -2.64) * mm});
            skLineSegment(sketch, "E133", {"start": v(22.7, -2.64) * mm, "end": v(22.83, -1.23) * mm});
            skLineSegment(sketch, "E134", {"start": v(22.83, -1.23) * mm, "end": v(22.85, -0.75) * mm});
            skLineSegment(sketch, "E135", {"start": v(22.85, -0.75) * mm, "end": v(2.76, -0.75) * mm});
            skLineSegment(sketch, "E136", {"start": v(2.76, -0.75) * mm, "end": v(2.68, -0.99) * mm});
            skLineSegment(sketch, "E137", {"start": v(2.68, -0.99) * mm, "end": v(2.56, -1.27) * mm});
            skLineSegment(sketch, "E138", {"start": v(2.56, -1.27) * mm, "end": v(2.42, -1.51) * mm});
            skLineSegment(sketch, "E139", {"start": v(2.42, -1.51) * mm, "end": v(2.24, -1.77) * mm});
            skLineSegment(sketch, "E140", {"start": v(2.24, -1.77) * mm, "end": v(2.05, -2) * mm});
            skLineSegment(sketch, "E141", {"start": v(2.05, -2) * mm, "end": v(1.8, -2.22) * mm});
            skLineSegment(sketch, "E142", {"start": v(1.8, -2.22) * mm, "end": v(1.6, -2.37) * mm});
            skLineSegment(sketch, "E143", {"start": v(1.6, -2.37) * mm, "end": v(1.36, -2.52) * mm});
            skLineSegment(sketch, "E144", {"start": v(1.36, -2.52) * mm, "end": v(1.1, -2.64) * mm});
            skSolve(sketch);
        }
        {
            var Q0;
            Q0 = qSketchRegion(id + "F32", true);
            extrude(context, id + "F33", {"entities" : qUnion([Q0]), "operationType" : NewBodyOperationType.REMOVE, "oppositeDirection" : true, "depth" : 5.08 * mm, "offsetDistance" : 25.4 * mm});
        }
        {
            var Q0;
            Q0=makeQuery(id+"F30.boolean.opBoolean","MERGE",FACE,{"derivedFrom":[makeQuery(id+"F11.boolean.opBoolean","MERGE",FACE,{"derivedFrom":[makeQuery(id+"F5.boolean.opBoolean","COPY",FACE,{"derivedFrom":makeQuery(id+"F5.opExtrude","CAP_FACE",FACE,{"disambiguationData":[OSD([sQuery(id+"F4.wireOp",EDGE,"E2"),sQuery(id+"F4.wireOp",EDGE,"E3")])],"isStart":false})}),makeQuery(id+"F11.opExtrude","CAP_FACE",FACE,{"disambiguationData":[OSD([sQuery(id+"F10.wireOp",EDGE,"E8.bottom"),sQuery(id+"F10.wireOp",EDGE,"E8.top"),sQuery(id+"F10.wireOp",EDGE,"E8.left"),sQuery(id+"F10.wireOp",EDGE,"E8.right"),sQuery(id+"F10.wireOp",EDGE,"E9.bottom"),sQuery(id+"F10.wireOp",EDGE,"E9.top"),sQuery(id+"F10.wireOp",EDGE,"E9.right")])],"isStart":false})]}),makeQuery(id+"F30.opExtrude","CAP_FACE",FACE,{"disambiguationData":[OSD([sQuery(id+"F29.wireOp",EDGE,"E33.bottom"),sQuery(id+"F29.wireOp",EDGE,"E33.top"),sQuery(id+"F29.wireOp",EDGE,"E33.left"),sQuery(id+"F29.wireOp",EDGE,"E33.right")])],"isStart":false})]});
            var sketch = newSketch(context, id + "F34", { "sketchPlane" : qUnion([Q0])});
            skCircle(sketch, "E145", {"center": v(0, 0) * mm, "radius": 30.1 * mm});
            skCircle(sketch, "E146", {"center": v(0, -60.2) * mm, "radius": 30.1 * mm});
            skSolve(sketch);
        }
        {
            var Q0;
            Q0 = qSketchRegion(id + "F34", true);
            extrude(context, id + "F35", {"entities" : qUnion([Q0]), "depth" : 8 * mm, "offsetDistance" : 25.4 * mm});
        }
        {
            var Q0;
            {var subQ0=sQuery(id+"F0.wireOp",EDGE,"E0.right");Q0=makeQuery(id+"F30.boolean.opBoolean","INTERSECT",EDGE,{"derivedFrom":[makeQuery(id+"F12.boolean.opBoolean","MERGE",FACE,{"derivedFrom":[makeQuery(id+"F1.opExtrude","SWEPT_FACE",FACE,{"disambiguationData":[OSD([subQ0])]}),makeQuery(id+"F12.opExtrude","SWEPT_FACE",FACE,{"disambiguationData":[OSD([subQ0])]})]}),makeQuery(id+"F30.opExtrude","SWEPT_FACE",FACE,{"disambiguationData":[OSD([sQuery(id+"F29.wireOp",EDGE,"E33.top")])]})]});}
            var Q1;
            Q1=makeQuery(id+"F30.boolean.opBoolean","INTERSECT",EDGE,{"derivedFrom":[makeQuery(id+"F3.opExtrude","SWEPT_FACE",FACE,{"disambiguationData":[OSD([sQuery(id+"F2.wireOp",EDGE,"E1.left")])]}),makeQuery(id+"F30.opExtrude","SWEPT_FACE",FACE,{"disambiguationData":[OSD([sQuery(id+"F29.wireOp",EDGE,"E33.top")])]})]});
            var Q2;
            {var subQ0=sQuery(id+"F0.wireOp",EDGE,"E0.right");Q2=makeQuery(id+"F30.boolean.opBoolean","INTERSECT",EDGE,{"derivedFrom":[makeQuery(id+"F12.boolean.opBoolean","MERGE",FACE,{"derivedFrom":[makeQuery(id+"F1.opExtrude","SWEPT_FACE",FACE,{"disambiguationData":[OSD([subQ0])]}),makeQuery(id+"F12.opExtrude","SWEPT_FACE",FACE,{"disambiguationData":[OSD([subQ0])]})]}),makeQuery(id+"F30.opExtrude","SWEPT_FACE",FACE,{"disambiguationData":[OSD([sQuery(id+"F29.wireOp",EDGE,"E33.bottom")])]})]});}
            var Q3;
            Q3=makeQuery(id+"F30.boolean.opBoolean","INTERSECT",EDGE,{"derivedFrom":[makeQuery(id+"F3.opExtrude","SWEPT_FACE",FACE,{"disambiguationData":[OSD([sQuery(id+"F2.wireOp",EDGE,"E1.left")])]}),makeQuery(id+"F30.opExtrude","SWEPT_FACE",FACE,{"disambiguationData":[OSD([sQuery(id+"F29.wireOp",EDGE,"E33.bottom")])]})]});
            fillet(context, id + "F36", {"entities" : qUnion([Q0, Q1, Q2, Q3]), "radius" : 7.62 * mm, "tangentPropagation" : true, "allowEdgeOverflow" : false});
        }
        {
            var Q0;
            {var subQ1=sQuery(id+"F2.wireOp",EDGE,"E1.right");var subQ2=sQuery(id+"F2.wireOp",EDGE,"E1.left");var subQ3=sQuery(id+"F2.wireOp",EDGE,"E1.top");var subQ4=sQuery(id+"F2.wireOp",EDGE,"E1.bottom");var subQ5=makeQuery(id+"F3.opExtrude","CAP_FACE",FACE,{"disambiguationData":[OSD([subQ4,subQ3,subQ2,subQ1])],"isStart":true});Q0=makeQuery(id+"F30.boolean.opBoolean","SPLIT",FACE,{"disambiguationData":[TD([makeQuery(id+"F3.opExtrude","SWEPT_FACE",FACE,{"disambiguationData":[OSD([subQ4])]})])],"derivedFrom":subQ5});}
            var sketch = newSketch(context, id + "F37", { "sketchPlane" : qUnion([Q0])});
            skLineSegment(sketch, "E147", {"start": v(-21.42, 33.44) * mm, "end": v(-23.94, 35.67) * mm});
            skLineSegment(sketch, "E148", {"start": v(-23.94, 35.67) * mm, "end": v(-32.18, 35.94) * mm});
            skLineSegment(sketch, "E149", {"start": v(-32.18, 35.94) * mm, "end": v(-35.44, 36.4) * mm});
            skLineSegment(sketch, "E150", {"start": v(-35.44, 36.4) * mm, "end": v(-37.5, 38.56) * mm});
            skLineSegment(sketch, "E151", {"start": v(-37.5, 38.56) * mm, "end": v(-37.9, 41.24) * mm});
            skLineSegment(sketch, "E152", {"start": v(-37.9, 41.24) * mm, "end": v(-50.12, 47.57) * mm});
            skLineSegment(sketch, "E153", {"start": v(-50.12, 47.57) * mm, "end": v(-51.95, 46.49) * mm});
            skLineSegment(sketch, "E154", {"start": v(-51.95, 46.49) * mm, "end": v(-55.16, 46.49) * mm});
            skLineSegment(sketch, "E155", {"start": v(-55.16, 46.49) * mm, "end": v(-56.94, 47.52) * mm});
            skLineSegment(sketch, "E156", {"start": v(-56.94, 47.52) * mm, "end": v(-58, 48.84) * mm});
            skLineSegment(sketch, "E157", {"start": v(-58, 48.84) * mm, "end": v(-58.58, 50.52) * mm});
            skLineSegment(sketch, "E158", {"start": v(-58.58, 50.52) * mm, "end": v(-58.58, 52.1) * mm});
            skLineSegment(sketch, "E159", {"start": v(-58.58, 52.1) * mm, "end": v(-57.94, 53.88) * mm});
            skLineSegment(sketch, "E160", {"start": v(-57.94, 53.88) * mm, "end": v(-69.04, 73.5) * mm});
            skLineSegment(sketch, "E161", {"start": v(-69.04, 73.5) * mm, "end": v(-69.15, 75.37) * mm});
            skLineSegment(sketch, "E162", {"start": v(-69.15, 75.37) * mm, "end": v(-68.78, 76.64) * mm});
            skLineSegment(sketch, "E163", {"start": v(-68.78, 76.64) * mm, "end": v(-68.18, 77.63) * mm});
            skLineSegment(sketch, "E164", {"start": v(-68.18, 77.63) * mm, "end": v(-67.37, 78.44) * mm});
            skLineSegment(sketch, "E165", {"start": v(-67.37, 78.44) * mm, "end": v(-66.12, 79.15) * mm});
            skLineSegment(sketch, "E166", {"start": v(-66.12, 79.15) * mm, "end": v(-64.44, 79.46) * mm});
            skLineSegment(sketch, "E167", {"start": v(-64.44, 79.46) * mm, "end": v(-63.06, 79.26) * mm});
            skLineSegment(sketch, "E168", {"start": v(-63.06, 79.26) * mm, "end": v(-61.52, 78.47) * mm});
            skLineSegment(sketch, "E169", {"start": v(-61.52, 78.47) * mm, "end": v(-60.43, 77.28) * mm});
            skLineSegment(sketch, "E170", {"start": v(-60.43, 77.28) * mm, "end": v(-59.77, 75.69) * mm});
            skLineSegment(sketch, "E171", {"start": v(-59.77, 75.69) * mm, "end": v(-59.7, 74.15) * mm});
            skLineSegment(sketch, "E172", {"start": v(-59.7, 74.15) * mm, "end": v(-60.47, 72.05) * mm});
            skLineSegment(sketch, "E173", {"start": v(-60.47, 72.05) * mm, "end": v(-61.68, 70.81) * mm});
            skLineSegment(sketch, "E174", {"start": v(-61.68, 70.81) * mm, "end": v(-63.48, 70.03) * mm});
            skLineSegment(sketch, "E175", {"start": v(-63.48, 70.03) * mm, "end": v(-64.9, 69.96) * mm});
            skLineSegment(sketch, "E176", {"start": v(-64.9, 69.96) * mm, "end": v(-66.87, 70.6) * mm});
            skLineSegment(sketch, "E177", {"start": v(-66.87, 70.6) * mm, "end": v(-57.65, 54.32) * mm});
            skLineSegment(sketch, "E178", {"start": v(-57.65, 54.32) * mm, "end": v(-57.04, 55) * mm});
            skLineSegment(sketch, "E179", {"start": v(-57.04, 55) * mm, "end": v(-56.23, 55.63) * mm});
            skLineSegment(sketch, "E180", {"start": v(-56.23, 55.63) * mm, "end": v(-55.35, 56.06) * mm});
            skLineSegment(sketch, "E181", {"start": v(-55.35, 56.06) * mm, "end": v(-54.52, 56.3) * mm});
            skLineSegment(sketch, "E182", {"start": v(-54.52, 56.3) * mm, "end": v(-53.56, 56.48) * mm});
            skLineSegment(sketch, "E183", {"start": v(-53.56, 56.48) * mm, "end": v(-52.6, 56.3) * mm});
            skLineSegment(sketch, "E184", {"start": v(-52.6, 56.3) * mm, "end": v(-51.14, 55.78) * mm});
            skLineSegment(sketch, "E185", {"start": v(-51.14, 55.78) * mm, "end": v(-50.25, 55.3) * mm});
            skLineSegment(sketch, "E186", {"start": v(-50.25, 55.3) * mm, "end": v(-49.1, 53.88) * mm});
            skLineSegment(sketch, "E187", {"start": v(-49.1, 53.88) * mm, "end": v(-48.82, 53.13) * mm});
            skLineSegment(sketch, "E188", {"start": v(-48.82, 53.13) * mm, "end": v(-48.6, 52.4) * mm});
            skLineSegment(sketch, "E189", {"start": v(-48.6, 52.4) * mm, "end": v(-48.48, 51.08) * mm});
            skLineSegment(sketch, "E190", {"start": v(-48.48, 51.08) * mm, "end": v(-48.64, 50.03) * mm});
            skLineSegment(sketch, "E191", {"start": v(-48.64, 50.03) * mm, "end": v(-48.95, 49.17) * mm});
            skLineSegment(sketch, "E192", {"start": v(-48.95, 49.17) * mm, "end": v(-49.7, 48) * mm});
            skLineSegment(sketch, "E193", {"start": v(-49.7, 48) * mm, "end": v(-37.8, 41.77) * mm});
            skLineSegment(sketch, "E194", {"start": v(-37.8, 41.77) * mm, "end": v(-37.63, 42.32) * mm});
            skLineSegment(sketch, "E195", {"start": v(-37.63, 42.32) * mm, "end": v(-37.42, 42.79) * mm});
            skLineSegment(sketch, "E196", {"start": v(-37.42, 42.79) * mm, "end": v(-37.08, 43.34) * mm});
            skLineSegment(sketch, "E197", {"start": v(-37.08, 43.34) * mm, "end": v(-36.73, 43.78) * mm});
            skLineSegment(sketch, "E198", {"start": v(-36.73, 43.78) * mm, "end": v(-36.23, 44.25) * mm});
            skLineSegment(sketch, "E199", {"start": v(-36.23, 44.25) * mm, "end": v(-35.56, 44.72) * mm});
            skLineSegment(sketch, "E200", {"start": v(-35.56, 44.72) * mm, "end": v(-34.61, 45.14) * mm});
            skLineSegment(sketch, "E201", {"start": v(-34.61, 45.14) * mm, "end": v(-33.52, 45.34) * mm});
            skLineSegment(sketch, "E202", {"start": v(-33.52, 45.34) * mm, "end": v(-31.7, 45.7) * mm});
            skLineSegment(sketch, "E203", {"start": v(-31.7, 45.7) * mm, "end": v(-31.41, 46.48) * mm});
            skLineSegment(sketch, "E204", {"start": v(-31.41, 46.48) * mm, "end": v(-31.89, 47.57) * mm});
            skLineSegment(sketch, "E205", {"start": v(-31.89, 47.57) * mm, "end": v(-32.28, 48.68) * mm});
            skLineSegment(sketch, "E206", {"start": v(-32.28, 48.68) * mm, "end": v(-33.19, 51.64) * mm});
            skLineSegment(sketch, "E207", {"start": v(-33.19, 51.64) * mm, "end": v(-33.77, 53.88) * mm});
            skLineSegment(sketch, "E208", {"start": v(-33.77, 53.88) * mm, "end": v(-34.18, 57.67) * mm});
            skLineSegment(sketch, "E209", {"start": v(-34.18, 57.67) * mm, "end": v(-34.26, 61.34) * mm});
            skLineSegment(sketch, "E210", {"start": v(-34.26, 61.34) * mm, "end": v(-33.85, 65.6) * mm});
            skLineSegment(sketch, "E211", {"start": v(-33.85, 65.6) * mm, "end": v(-33, 69.43) * mm});
            skLineSegment(sketch, "E212", {"start": v(-33, 69.43) * mm, "end": v(-32.37, 71.47) * mm});
            skLineSegment(sketch, "E213", {"start": v(-32.37, 71.47) * mm, "end": v(-31.23, 74.33) * mm});
            skLineSegment(sketch, "E214", {"start": v(-31.23, 74.33) * mm, "end": v(-29.69, 77.33) * mm});
            skLineSegment(sketch, "E215", {"start": v(-29.69, 77.33) * mm, "end": v(-27.76, 80.3) * mm});
            skLineSegment(sketch, "E216", {"start": v(-27.76, 80.3) * mm, "end": v(-25.08, 83.56) * mm});
            skLineSegment(sketch, "E217", {"start": v(-25.08, 83.56) * mm, "end": v(-20.4, 87.74) * mm});
            skLineSegment(sketch, "E218", {"start": v(-20.4, 87.74) * mm, "end": v(-15.15, 90.94) * mm});
            skLineSegment(sketch, "E219", {"start": v(-15.15, 90.94) * mm, "end": v(-11.15, 92.6) * mm});
            skLineSegment(sketch, "E220", {"start": v(-11.15, 92.6) * mm, "end": v(-6.31, 93.89) * mm});
            skLineSegment(sketch, "E221", {"start": v(-6.31, 93.89) * mm, "end": v(-1.15, 94.45) * mm});
            skLineSegment(sketch, "E222", {"start": v(-1.15, 94.45) * mm, "end": v(4.49, 94.18) * mm});
            skLineSegment(sketch, "E223", {"start": v(4.49, 94.18) * mm, "end": v(9.82, 93.04) * mm});
            skLineSegment(sketch, "E224", {"start": v(9.82, 93.04) * mm, "end": v(14.87, 91.08) * mm});
            skLineSegment(sketch, "E225", {"start": v(14.87, 91.08) * mm, "end": v(19.66, 88.28) * mm});
            skLineSegment(sketch, "E226", {"start": v(19.66, 88.28) * mm, "end": v(24.32, 84.35) * mm});
            skLineSegment(sketch, "E227", {"start": v(24.32, 84.35) * mm, "end": v(28.04, 79.91) * mm});
            skLineSegment(sketch, "E228", {"start": v(28.04, 79.91) * mm, "end": v(31, 74.83) * mm});
            skLineSegment(sketch, "E229", {"start": v(31, 74.83) * mm, "end": v(32.83, 70.03) * mm});
            skLineSegment(sketch, "E230", {"start": v(32.83, 70.03) * mm, "end": v(33.97, 64.78) * mm});
            skLineSegment(sketch, "E231", {"start": v(33.97, 64.78) * mm, "end": v(33.97, 98.66) * mm});
            skLineSegment(sketch, "E232", {"start": v(33.97, 98.66) * mm, "end": v(-71.22, 98.66) * mm});
            skLineSegment(sketch, "E233", {"start": v(-71.22, 98.66) * mm, "end": v(-71.22, 38.56) * mm});
            skLineSegment(sketch, "E234", {"start": v(-71.22, 38.56) * mm, "end": v(-70.67, 36.13) * mm});
            skLineSegment(sketch, "E235", {"start": v(-70.67, 36.13) * mm, "end": v(-69.65, 34.33) * mm});
            skLineSegment(sketch, "E236", {"start": v(-69.65, 34.33) * mm, "end": v(-68.79, 33.27) * mm});
            skLineSegment(sketch, "E237", {"start": v(-68.79, 33.27) * mm, "end": v(-67.4, 32.55) * mm});
            skLineSegment(sketch, "E238", {"start": v(-67.4, 32.55) * mm, "end": v(-65.63, 32.1) * mm});
            skLineSegment(sketch, "E239", {"start": v(-65.63, 32.1) * mm, "end": v(-19.64, 32.1) * mm});
            skLineSegment(sketch, "E240", {"start": v(-19.64, 32.1) * mm, "end": v(-21.42, 33.44) * mm});
            skSolve(sketch);
        }
        {
            var Q0;
            Q0 = qSketchRegion(id + "F37", true);
            extrude(context, id + "F38", {"entities" : qUnion([Q0]), "operationType" : NewBodyOperationType.REMOVE, "oppositeDirection" : true, "depth" : 4.2 * mm, "offsetDistance" : 25.4 * mm});
        }
        {
            var Q0;
            {var subQ1=sQuery(id+"F2.wireOp",EDGE,"E1.right");var subQ2=sQuery(id+"F2.wireOp",EDGE,"E1.left");var subQ3=sQuery(id+"F2.wireOp",EDGE,"E1.top");var subQ4=sQuery(id+"F2.wireOp",EDGE,"E1.bottom");var subQ5=makeQuery(id+"F3.opExtrude","CAP_FACE",FACE,{"disambiguationData":[OSD([subQ4,subQ3,subQ2,subQ1])],"isStart":true});Q0=makeQuery(id+"F30.boolean.opBoolean","SPLIT",FACE,{"disambiguationData":[TD([makeQuery(id+"F3.opExtrude","SWEPT_FACE",FACE,{"disambiguationData":[OSD([subQ3])]})])],"derivedFrom":subQ5});}
            var sketch = newSketch(context, id + "F39", { "sketchPlane" : qUnion([Q0])});
            skLineSegment(sketch, "E241", {"start": v(-21.99, 26.47) * mm, "end": v(-59.7, 26.47) * mm});
            skLineSegment(sketch, "E242", {"start": v(-59.7, 26.47) * mm, "end": v(-59.67, 19.98) * mm});
            skLineSegment(sketch, "E243", {"start": v(-59.67, 19.98) * mm, "end": v(-60.48, 17.29) * mm});
            skLineSegment(sketch, "E244", {"start": v(-60.48, 17.29) * mm, "end": v(-62.22, 15.73) * mm});
            skLineSegment(sketch, "E245", {"start": v(-62.22, 15.73) * mm, "end": v(-66.64, 15.73) * mm});
            skLineSegment(sketch, "E246", {"start": v(-66.64, 15.73) * mm, "end": v(-68.52, 17.51) * mm});
            skLineSegment(sketch, "E247", {"start": v(-68.52, 17.51) * mm, "end": v(-70.85, 18.9) * mm});
            skLineSegment(sketch, "E248", {"start": v(-70.85, 18.9) * mm, "end": v(-70.85, 15.73) * mm});
            skLineSegment(sketch, "E249", {"start": v(-70.85, 15.73) * mm, "end": v(-70.85, 14.3) * mm});
            skLineSegment(sketch, "E250", {"start": v(-70.85, 14.3) * mm, "end": v(-21.94, -34.6) * mm});
            skLineSegment(sketch, "E251", {"start": v(-21.94, -34.6) * mm, "end": v(-2.79, -34.3) * mm});
            skLineSegment(sketch, "E252", {"start": v(-2.79, -34.3) * mm, "end": v(-9.16, -33.17) * mm});
            skLineSegment(sketch, "E253", {"start": v(-9.16, -33.17) * mm, "end": v(-14.08, -31.4) * mm});
            skLineSegment(sketch, "E254", {"start": v(-14.08, -31.4) * mm, "end": v(-18.77, -28.84) * mm});
            skLineSegment(sketch, "E255", {"start": v(-18.77, -28.84) * mm, "end": v(-21.94, -26.5) * mm});
            skLineSegment(sketch, "E256", {"start": v(-21.94, -26.5) * mm, "end": v(-25.09, -23.55) * mm});
            skLineSegment(sketch, "E257", {"start": v(-25.09, -23.55) * mm, "end": v(-27.44, -20.76) * mm});
            skLineSegment(sketch, "E258", {"start": v(-27.44, -20.76) * mm, "end": v(-29.73, -17.33) * mm});
            skLineSegment(sketch, "E259", {"start": v(-29.73, -17.33) * mm, "end": v(-31.18, -14.56) * mm});
            skLineSegment(sketch, "E260", {"start": v(-31.18, -14.56) * mm, "end": v(-32.48, -11.37) * mm});
            skLineSegment(sketch, "E261", {"start": v(-32.48, -11.37) * mm, "end": v(-33.33, -8.57) * mm});
            skLineSegment(sketch, "E262", {"start": v(-33.33, -8.57) * mm, "end": v(-34.07, -4.82) * mm});
            skLineSegment(sketch, "E263", {"start": v(-34.07, -4.82) * mm, "end": v(-34.36, -1.84) * mm});
            skLineSegment(sketch, "E264", {"start": v(-34.36, -1.84) * mm, "end": v(-34.35, 1.98) * mm});
            skLineSegment(sketch, "E265", {"start": v(-34.35, 1.98) * mm, "end": v(-33.86, 6.12) * mm});
            skLineSegment(sketch, "E266", {"start": v(-33.86, 6.12) * mm, "end": v(-32.98, 9.82) * mm});
            skLineSegment(sketch, "E267", {"start": v(-32.98, 9.82) * mm, "end": v(-31.57, 13.68) * mm});
            skLineSegment(sketch, "E268", {"start": v(-31.57, 13.68) * mm, "end": v(-29.62, 17.51) * mm});
            skLineSegment(sketch, "E269", {"start": v(-29.62, 17.51) * mm, "end": v(-27.02, 21.3) * mm});
            skLineSegment(sketch, "E270", {"start": v(-27.02, 21.3) * mm, "end": v(-24.46, 24.2) * mm});
            skLineSegment(sketch, "E271", {"start": v(-24.46, 24.2) * mm, "end": v(-21.99, 26.47) * mm});
            skLineSegment(sketch, "E272", {"start": v(4.2, -34.15) * mm, "end": v(10.12, -32.89) * mm});
            skLineSegment(sketch, "E273", {"start": v(10.12, -32.89) * mm, "end": v(15.8, -30.56) * mm});
            skLineSegment(sketch, "E274", {"start": v(15.8, -30.56) * mm, "end": v(20.8, -27.42) * mm});
            skLineSegment(sketch, "E275", {"start": v(20.8, -27.42) * mm, "end": v(26.03, -22.5) * mm});
            skLineSegment(sketch, "E276", {"start": v(26.03, -22.5) * mm, "end": v(29.24, -18.15) * mm});
            skLineSegment(sketch, "E277", {"start": v(29.24, -18.15) * mm, "end": v(30.94, -15.05) * mm});
            skLineSegment(sketch, "E278", {"start": v(30.94, -15.05) * mm, "end": v(33.54, -7.7) * mm});
            skLineSegment(sketch, "E279", {"start": v(33.54, -7.7) * mm, "end": v(32.9, -25.49) * mm});
            skLineSegment(sketch, "E280", {"start": v(32.9, -25.49) * mm, "end": v(31.72, -24.36) * mm});
            skLineSegment(sketch, "E281", {"start": v(31.72, -24.36) * mm, "end": v(30.22, -23.7) * mm});
            skLineSegment(sketch, "E282", {"start": v(30.22, -23.7) * mm, "end": v(28.77, -23.58) * mm});
            skLineSegment(sketch, "E283", {"start": v(28.77, -23.58) * mm, "end": v(27.23, -23.94) * mm});
            skLineSegment(sketch, "E284", {"start": v(27.23, -23.94) * mm, "end": v(25.69, -25) * mm});
            skLineSegment(sketch, "E285", {"start": v(25.69, -25) * mm, "end": v(24.69, -26.51) * mm});
            skLineSegment(sketch, "E286", {"start": v(24.69, -26.51) * mm, "end": v(24.34, -28.73) * mm});
            skLineSegment(sketch, "E287", {"start": v(24.34, -28.73) * mm, "end": v(24.89, -30.57) * mm});
            skLineSegment(sketch, "E288", {"start": v(24.89, -30.57) * mm, "end": v(26.17, -32.09) * mm});
            skLineSegment(sketch, "E289", {"start": v(26.17, -32.09) * mm, "end": v(27.72, -32.89) * mm});
            skLineSegment(sketch, "E290", {"start": v(27.72, -32.89) * mm, "end": v(27.9, -34.66) * mm});
            skLineSegment(sketch, "E291", {"start": v(27.9, -34.66) * mm, "end": v(4.2, -34.15) * mm});
            skSolve(sketch);
        }
        {
            var Q0;
            Q0 = qSketchRegion(id + "F39", true);
            extrude(context, id + "F40", {"entities" : qUnion([Q0]), "operationType" : NewBodyOperationType.REMOVE, "oppositeDirection" : true, "depth" : 4.2 * mm, "offsetDistance" : 25.4 * mm});
        }
        {
            var Q0;
            {var subQ1=sQuery(id+"F2.wireOp",EDGE,"E1.right");var subQ2=sQuery(id+"F2.wireOp",EDGE,"E1.left");var subQ3=sQuery(id+"F2.wireOp",EDGE,"E1.top");var subQ4=sQuery(id+"F2.wireOp",EDGE,"E1.bottom");var subQ5=makeQuery(id+"F3.opExtrude","CAP_FACE",FACE,{"disambiguationData":[OSD([subQ4,subQ3,subQ2,subQ1])],"isStart":true});Q0=makeQuery(id+"F30.boolean.opBoolean","SPLIT",FACE,{"disambiguationData":[TD([makeQuery(id+"F3.opExtrude","SWEPT_FACE",FACE,{"disambiguationData":[OSD([subQ4])]})])],"derivedFrom":subQ5});}
            var sketch = newSketch(context, id + "F41", { "sketchPlane" : qUnion([Q0])});
            skLineSegment(sketch, "E292", {"start": v(-61.89, 68.28) * mm, "end": v(-68.47, 71.41) * mm});
            skLineSegment(sketch, "E293", {"start": v(-68.47, 71.41) * mm, "end": v(-59, 51.1) * mm});
            skLineSegment(sketch, "E294", {"start": v(-59, 51.1) * mm, "end": v(-56.83, 56.58) * mm});
            skLineSegment(sketch, "E295", {"start": v(-56.83, 56.58) * mm, "end": v(-51.82, 57.16) * mm});
            skLineSegment(sketch, "E296", {"start": v(-51.82, 57.16) * mm, "end": v(-47.01, 52.97) * mm});
            skLineSegment(sketch, "E297", {"start": v(-47.01, 52.97) * mm, "end": v(-49.13, 48.6) * mm});
            skPoint(sketch, "E297.endSnap0", {"position": v(-49.32, 48.6) * mm});
            skLineSegment(sketch, "E298", {"start": v(-49.13, 48.6) * mm, "end": v(-52.94, 44.55) * mm});
            skLineSegment(sketch, "E299", {"start": v(-52.94, 44.55) * mm, "end": v(-37.5, 38.33) * mm});
            skLineSegment(sketch, "E300", {"start": v(-37.5, 38.33) * mm, "end": v(-37.9, 41.24) * mm});
            skLineSegment(sketch, "E301", {"start": v(-37.9, 41.24) * mm, "end": v(-37.8, 41.77) * mm});
            skLineSegment(sketch, "E302", {"start": v(-37.8, 41.77) * mm, "end": v(-38.71, 45.33) * mm});
            skLineSegment(sketch, "E303", {"start": v(-38.71, 45.33) * mm, "end": v(-45.59, 58.75) * mm});
            skLineSegment(sketch, "E304", {"start": v(-45.59, 58.75) * mm, "end": v(-61.89, 68.28) * mm});
            skSolve(sketch);
        }
        {
            var Q0;
            Q0 = qSketchRegion(id + "F41", true);
            extrude(context, id + "F42", {"entities" : qUnion([Q0]), "operationType" : NewBodyOperationType.REMOVE, "oppositeDirection" : true, "depth" : 4.2 * mm, "offsetDistance" : 25.4 * mm});
        }
        {
            var Q0;
            {var subQ0=sQuery(id+"F0.wireOp",EDGE,"E0.top");Q0=makeQuery(id+"F12.boolean.opBoolean","MERGE",FACE,{"derivedFrom":[makeQuery(id+"F1.opExtrude","SWEPT_FACE",FACE,{"disambiguationData":[OSD([subQ0])]}),makeQuery(id+"F12.opExtrude","SWEPT_FACE",FACE,{"disambiguationData":[OSD([subQ0])]})]});}
            cPlane(context, id + "F43", {"entities" : qUnion([Q0]), "cplaneType" : CPlaneType.OFFSET, "offset" : 15.5 * mm, "oppositeDirection" : true, "width" : 152.4 * mm, "height" : 152.4 * mm});
        }
        {
            var Q0;
            Q0=qCreatedBy(id+"F43.planeOp",FACE);
            var sketch = newSketch(context, id + "F44", { "sketchPlane" : qUnion([Q0])});
            skLineSegment(sketch, "E305.bottom", {"start": v(-83, 12.5) * mm, "end": v(63.05, 12.5) * mm});
            skLineSegment(sketch, "E305.top", {"start": v(-83, -12.9) * mm, "end": v(63.05, -12.9) * mm});
            skLineSegment(sketch, "E305.left", {"start": v(-83, 12.5) * mm, "end": v(-83, -12.9) * mm});
            skLineSegment(sketch, "E305.right", {"start": v(63.05, 12.5) * mm, "end": v(63.05, -12.9) * mm});
            skSolve(sketch);
        }
        {
            var Q0;
            Q0 = qSketchRegion(id + "F44", true);
            extrude(context, id + "F45", {"entities" : qUnion([Q0]), "depth" : 38.1 * mm, "offsetDistance" : 25.4 * mm});
        }
        {
            var Q0;
            Q0=makeQuery(id+"F45.opExtrude","CAP_FACE",FACE,{"disambiguationData":[OSD([sQuery(id+"F44.wireOp",EDGE,"E305.bottom"),sQuery(id+"F44.wireOp",EDGE,"E305.top"),sQuery(id+"F44.wireOp",EDGE,"E305.left"),sQuery(id+"F44.wireOp",EDGE,"E305.right")])],"isStart":true});
            var sketch = newSketch(context, id + "F46", { "sketchPlane" : qUnion([Q0])});
            skLineSegment(sketch, "E306.bottom", {"start": v(-35.31, 10.18) * mm, "end": v(72.74, 10.18) * mm});
            skLineSegment(sketch, "E306.top", {"start": v(-35.31, -9.9) * mm, "end": v(72.74, -9.9) * mm});
            skLineSegment(sketch, "E306.left", {"start": v(-35.31, 10.18) * mm, "end": v(-35.31, -9.9) * mm});
            skLineSegment(sketch, "E306.right", {"start": v(72.74, 10.18) * mm, "end": v(72.74, -9.9) * mm});
            skSolve(sketch);
        }
        {
            var Q0;
            Q0 = qSketchRegion(id + "F46", true);
            extrude(context, id + "F47", {"entities" : qUnion([Q0]), "operationType" : NewBodyOperationType.REMOVE, "oppositeDirection" : true, "depth" : 15.77 * mm, "offsetDistance" : 25.4 * mm});
        }
    });
